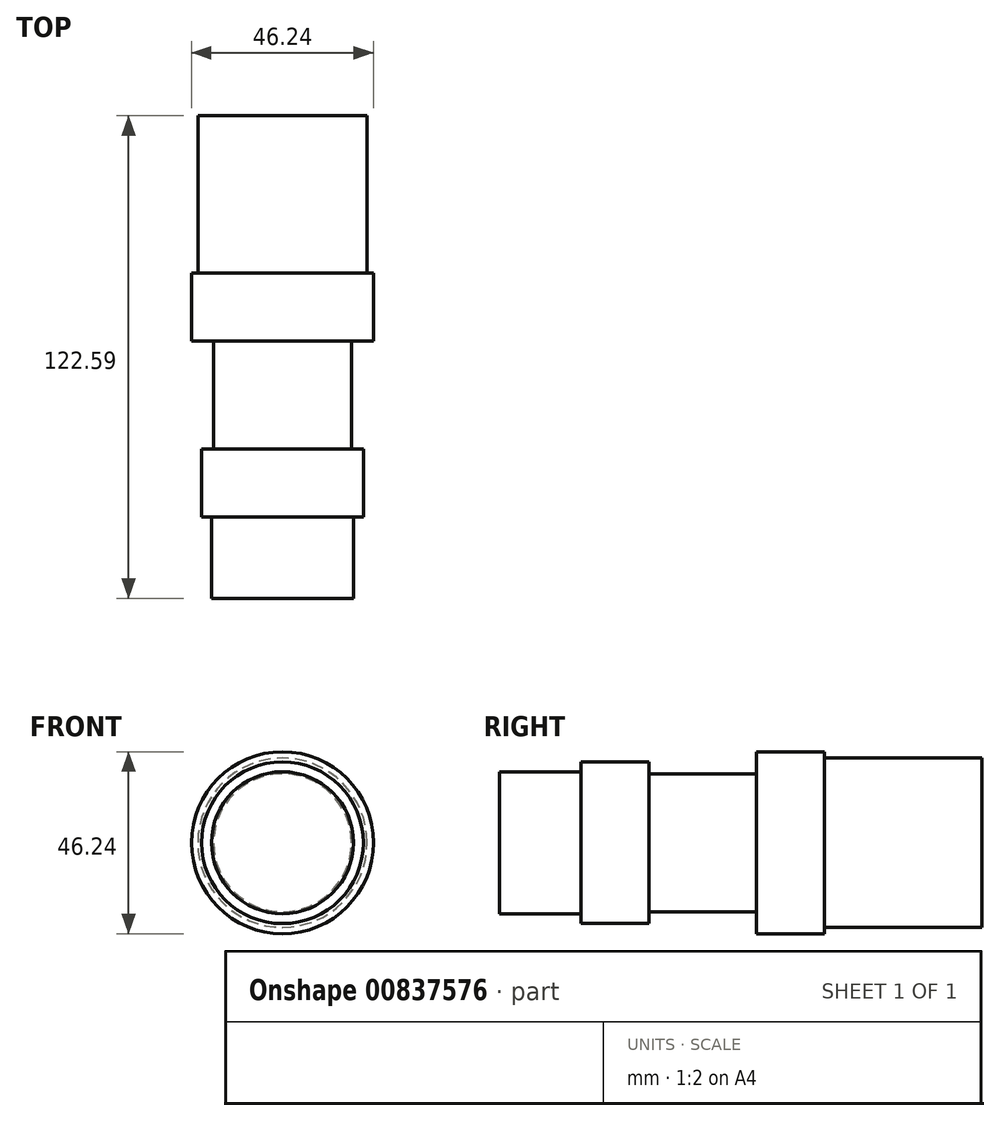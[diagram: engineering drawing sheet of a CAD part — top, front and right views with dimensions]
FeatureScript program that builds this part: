
annotation { "Feature Type Name" : "Feature", "Feature Type Description" : "" }
export const myFeature = defineFeature(function(context is Context, id is Id, definition is map)
    precondition{}
    {
        {
            var Q0;
            Q0=qCreatedBy(makeId("Front.planeOp"),FACE);
            var sketch = newSketch(context, id + "F0", { "sketchPlane" : qUnion([Q0])});
            skCircle(sketch, "E0", {"center": v(0, 0) * mm, "radius": 18.03 * mm});
            skSolve(sketch);
        }
        {
            var Q0;
            Q0=makeQuery(id+"F0.imprint","IMPRINT",FACE,{"disambiguationData":[TD([[makeQuery(id+"F0.imprint","IMPRINT",EDGE,{"derivedFrom":sQuery(id+"F0.wireOp",EDGE,"E0")}),1.0]])]});
            extrude(context, id + "F1", {"entities" : qUnion([Q0]), "oppositeDirection" : true, "depth" : 20.7 * mm, "offsetDistance" : 25 * mm});
        }
        {
            var Q0;
            Q0=makeQuery(id+"F1.opExtrude","CAP_FACE",FACE,{"disambiguationData":[OSD([sQuery(id+"F0.wireOp",EDGE,"E0")])],"isStart":false});
            cPlane(context, id + "F2", {"entities" : qUnion([Q0]), "cplaneType" : CPlaneType.OFFSET, "offset" : 0 * mm, "width" : 150 * mm, "height" : 150 * mm});
        }
        {
            var Q0;
            Q0=qCreatedBy(id+"F2.planeOp",FACE);
            var sketch = newSketch(context, id + "F3", { "sketchPlane" : qUnion([Q0])});
            skCircle(sketch, "E1", {"center": v(0, 0) * mm, "radius": 20.55 * mm});
            skSolve(sketch);
        }
        {
            var Q0;
            Q0=makeQuery(id+"F3.imprint","IMPRINT",FACE,{"disambiguationData":[TD([[makeQuery(id+"F3.imprint","IMPRINT",EDGE,{"derivedFrom":sQuery(id+"F3.wireOp",EDGE,"E1")}),1.0]])]});
            extrude(context, id + "F4", {"entities" : qUnion([Q0]), "operationType" : NewBodyOperationType.ADD, "depth" : 17.27 * mm, "offsetDistance" : 25 * mm});
        }
        {
            var Q0;
            Q0=makeQuery(id+"F4.opExtrude","CAP_FACE",FACE,{"disambiguationData":[OSD([sQuery(id+"F3.wireOp",EDGE,"E1")])],"isStart":false});
            cPlane(context, id + "F5", {"entities" : qUnion([Q0]), "cplaneType" : CPlaneType.OFFSET, "offset" : 0 * mm, "width" : 150 * mm, "height" : 150 * mm});
        }
        {
            var Q0;
            Q0=qCreatedBy(id+"F5.planeOp",FACE);
            var sketch = newSketch(context, id + "F6", { "sketchPlane" : qUnion([Q0])});
            skCircle(sketch, "E2", {"center": v(0, 0) * mm, "radius": 17.52 * mm});
            skSolve(sketch);
        }
        {
            var Q0;
            Q0=makeQuery(id+"F6.imprint","IMPRINT",FACE,{"disambiguationData":[TD([[makeQuery(id+"F6.imprint","IMPRINT",EDGE,{"derivedFrom":sQuery(id+"F6.wireOp",EDGE,"E2")}),1.0]])]});
            extrude(context, id + "F7", {"entities" : qUnion([Q0]), "operationType" : NewBodyOperationType.ADD, "depth" : 27.35 * mm, "offsetDistance" : 25 * mm});
        }
        {
            var Q0;
            Q0=makeQuery(id+"F7.opExtrude","CAP_FACE",FACE,{"disambiguationData":[OSD([sQuery(id+"F6.wireOp",EDGE,"E2")])],"isStart":false});
            cPlane(context, id + "F8", {"entities" : qUnion([Q0]), "cplaneType" : CPlaneType.OFFSET, "offset" : 0 * mm, "width" : 150 * mm, "height" : 150 * mm});
        }
        {
            var Q0;
            Q0=qCreatedBy(id+"F8.planeOp",FACE);
            var sketch = newSketch(context, id + "F9", { "sketchPlane" : qUnion([Q0])});
            skCircle(sketch, "E3", {"center": v(0, 0) * mm, "radius": 23.11 * mm});
            skSolve(sketch);
        }
        {
            var Q0;
            Q0=makeQuery(id+"F9.imprint","IMPRINT",FACE,{"disambiguationData":[TD([[makeQuery(id+"F9.imprint","IMPRINT",EDGE,{"derivedFrom":sQuery(id+"F9.wireOp",EDGE,"E3")}),1.0]])]});
            extrude(context, id + "F10", {"entities" : qUnion([Q0]), "operationType" : NewBodyOperationType.ADD, "depth" : 17.27 * mm, "offsetDistance" : 25 * mm});
        }
        {
            var Q0;
            Q0=makeQuery(id+"F10.opExtrude","CAP_FACE",FACE,{"disambiguationData":[OSD([sQuery(id+"F9.wireOp",EDGE,"E3")])],"isStart":false});
            cPlane(context, id + "F11", {"entities" : qUnion([Q0]), "cplaneType" : CPlaneType.OFFSET, "offset" : 0 * mm, "width" : 150 * mm, "height" : 150 * mm});
        }
        {
            var Q0;
            Q0=qCreatedBy(id+"F11.planeOp",FACE);
            var sketch = newSketch(context, id + "F12", { "sketchPlane" : qUnion([Q0])});
            skCircle(sketch, "E4", {"center": v(0, 0) * mm, "radius": 21.5 * mm});
            skSolve(sketch);
        }
        {
            var Q0;
            Q0=makeQuery(id+"F12.imprint","IMPRINT",FACE,{"disambiguationData":[TD([[makeQuery(id+"F12.imprint","IMPRINT",EDGE,{"derivedFrom":sQuery(id+"F12.wireOp",EDGE,"E4")}),1.0]])]});
            extrude(context, id + "F13", {"entities" : qUnion([Q0]), "operationType" : NewBodyOperationType.ADD, "depth" : 40 * mm, "offsetDistance" : 25 * mm});
        }
    });
